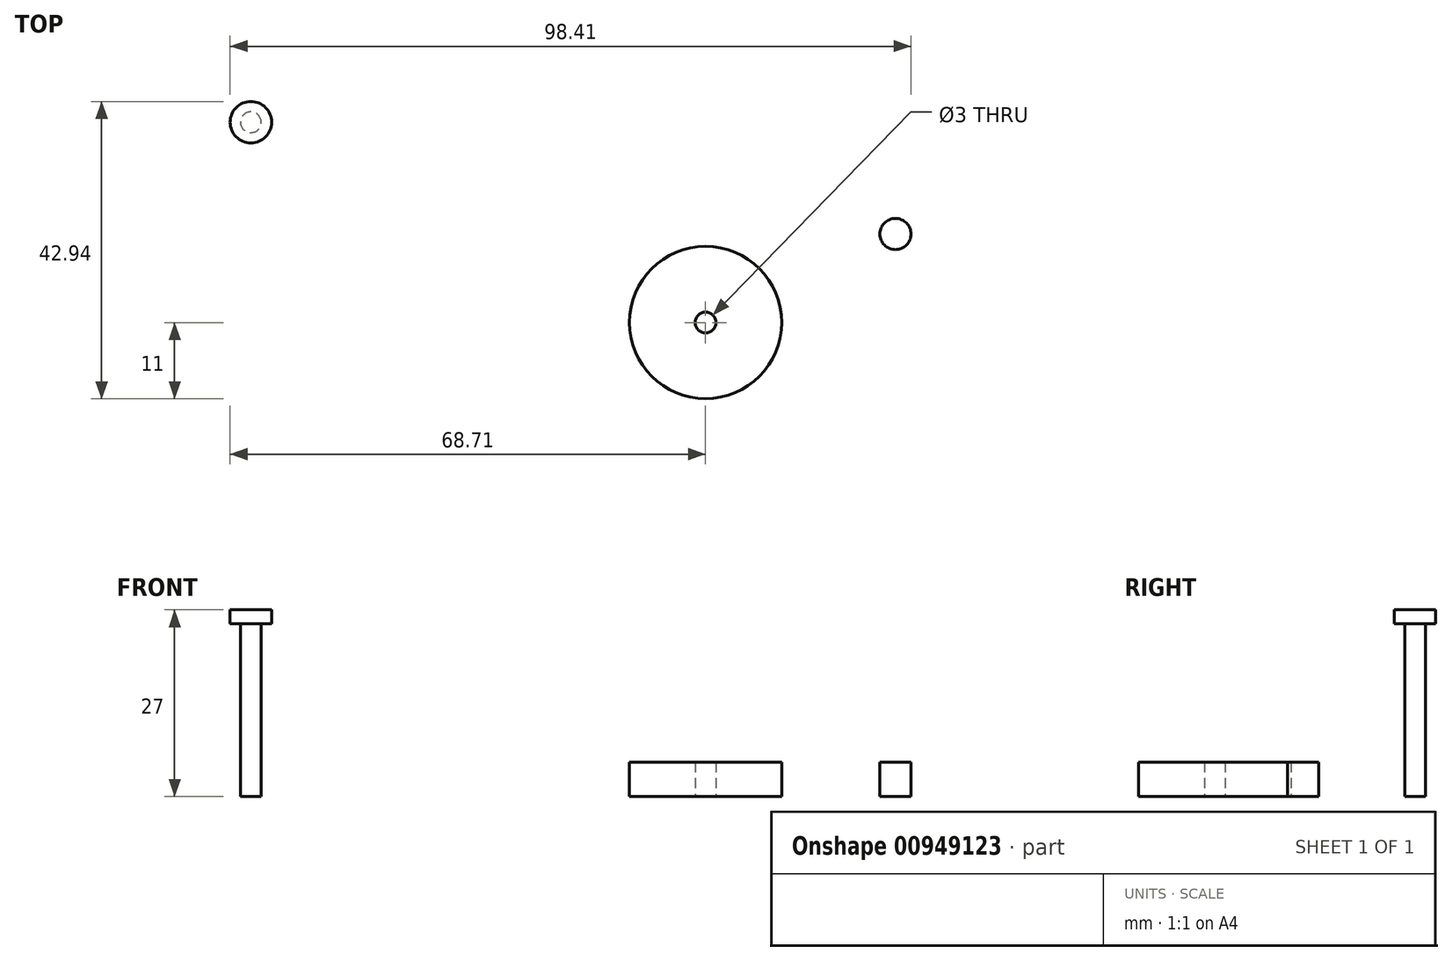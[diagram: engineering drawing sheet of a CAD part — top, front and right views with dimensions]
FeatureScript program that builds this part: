
annotation { "Feature Type Name" : "Feature", "Feature Type Description" : "" }
export const myFeature = defineFeature(function(context is Context, id is Id, definition is map)
    precondition{}
    {
        {
            var Q0;
            Q0=qCreatedBy(makeId("Top.planeOp"),FACE);
            var sketch = newSketch(context, id + "F0", { "sketchPlane" : qUnion([Q0])});
            skCircle(sketch, "E0", {"center": v(0, 0) * mm, "radius": 11 * mm});
            skCircle(sketch, "E1", {"center": v(27.45, 12.8) * mm, "radius": 2.25 * mm});
            skCircle(sketch, "E2", {"center": v(-65.7, 28.94) * mm, "radius": 1.5 * mm});
            skCircle(sketch, "E3", {"center": v(0, 0) * mm, "radius": 1.5 * mm});
            skSolve(sketch);
        }
        {
            var Q0;
            Q0=makeQuery(id+"F0.imprint","IMPRINT",FACE,{"disambiguationData":[TD([[makeQuery(id+"F0.imprint","IMPRINT",EDGE,{"derivedFrom":sQuery(id+"F0.wireOp",EDGE,"E0")}),1.0]])]});
            var Q1;
            Q1=makeQuery(id+"F0.imprint","IMPRINT",FACE,{"disambiguationData":[TD([[makeQuery(id+"F0.imprint","IMPRINT",EDGE,{"derivedFrom":sQuery(id+"F0.wireOp",EDGE,"E1")}),1.0]])]});
            extrude(context, id + "F1", {"entities" : qUnion([Q0, Q1]), "depth" : 5 * mm, "offsetDistance" : 25 * mm});
        }
        {
            var Q0;
            Q0=makeQuery(id+"F0.imprint","IMPRINT",FACE,{"disambiguationData":[TD([[makeQuery(id+"F0.imprint","IMPRINT",EDGE,{"derivedFrom":sQuery(id+"F0.wireOp",EDGE,"E2")}),1.0]])]});
            extrude(context, id + "F2", {"entities" : qUnion([Q0]), "depth" : 25 * mm, "offsetDistance" : 25 * mm});
        }
        {
            var Q0;
            Q0=makeQuery(id+"F2.opExtrude","CAP_FACE",FACE,{"disambiguationData":[OSD([sQuery(id+"F0.wireOp",EDGE,"E2")])],"isStart":false});
            var sketch = newSketch(context, id + "F3", { "sketchPlane" : qUnion([Q0])});
            skPoint(sketch, "E4", {"position": v(-64.53, 28.01) * mm});
            skPoint(sketch, "E5", {"position": v(-65.7, 28.94) * mm});
            skCircle(sketch, "E6", {"center": v(-65.7, 28.94) * mm, "radius": 3 * mm});
            skSolve(sketch);
        }
        {
            var Q0;
            Q0=makeQuery(id+"F3.imprint","IMPRINT",FACE,{"disambiguationData":[TD([[makeQuery(id+"F3.imprint","IMPRINT",EDGE,{"derivedFrom":sQuery(id+"F3.wireOp",EDGE,"E6")}),1.0]])]});
            var Q1;
            Q1=makeQuery(id+"F3.imprint","IMPRINT",FACE,{"disambiguationData":[TD([[makeQuery(id+"F3.imprint","IMPRINT",EDGE,{"derivedFrom":makeQuery(id+"F2.opExtrude","CAP_EDGE",EDGE,{"disambiguationData":[OSD([sQuery(id+"F0.wireOp",EDGE,"E2")])],"isStart":false})}),1.0]])]});
            extrude(context, id + "F4", {"entities" : qUnion([Q0, Q1]), "operationType" : NewBodyOperationType.ADD, "depth" : 2 * mm, "offsetDistance" : 25 * mm});
        }
    });
